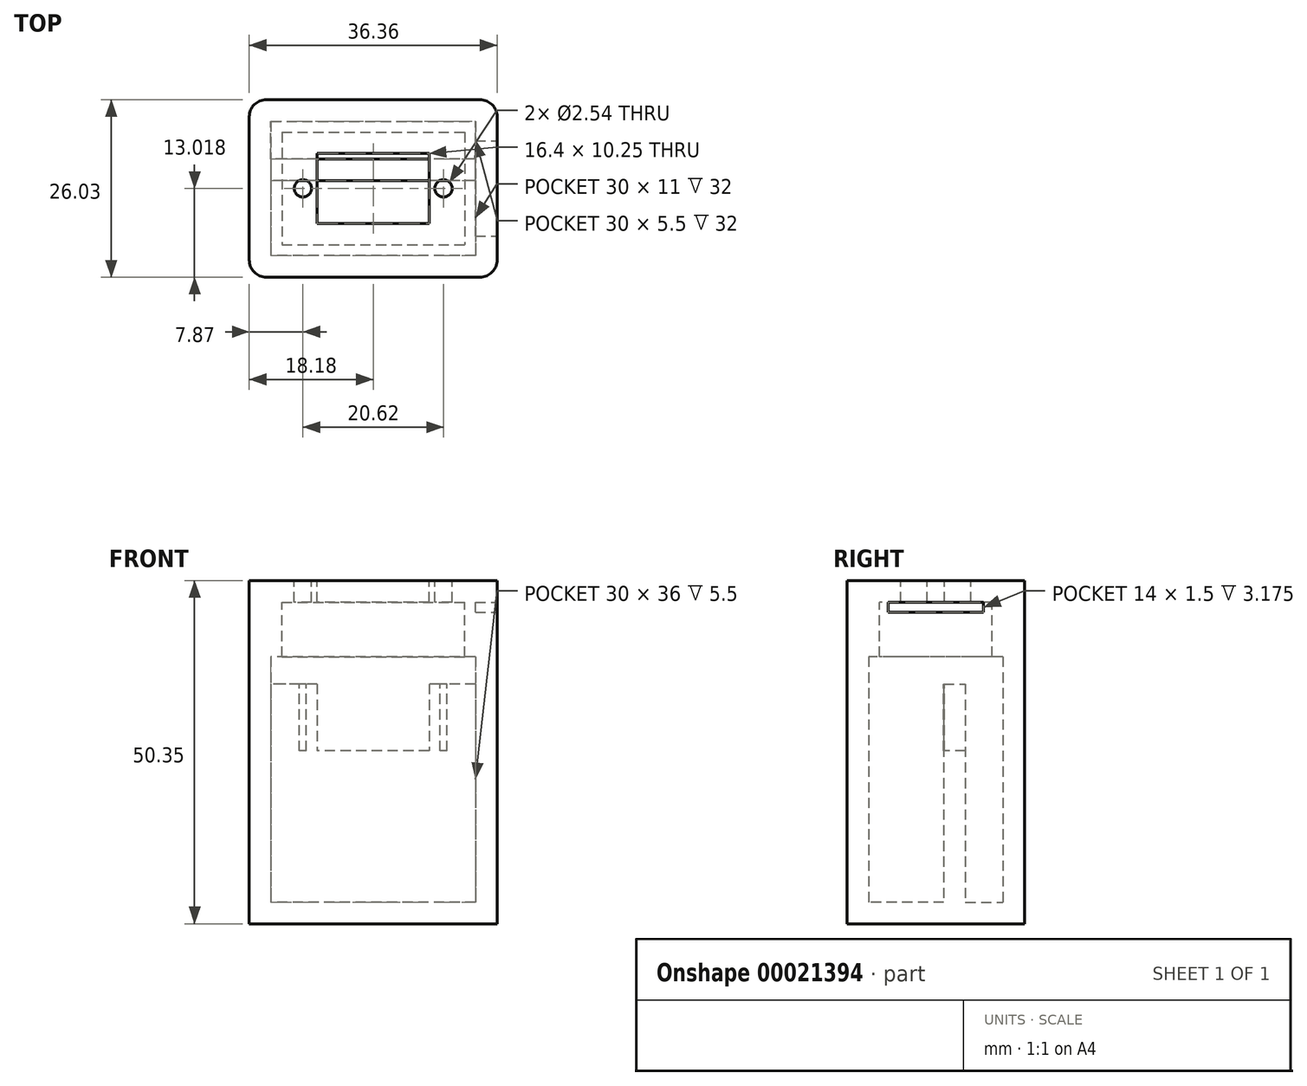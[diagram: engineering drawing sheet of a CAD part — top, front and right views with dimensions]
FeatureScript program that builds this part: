
annotation { "Feature Type Name" : "Feature", "Feature Type Description" : "" }
export const myFeature = defineFeature(function(context is Context, id is Id, definition is map)
    precondition{}
    {
        {
            var Q0;
            Q0=qCreatedBy(makeId("Top.planeOp"),FACE);
            var sketch = newSketch(context, id + "F0", { "sketchPlane" : qUnion([Q0])});
            skLineSegment(sketch, "E0.rect.bottom", {"start": v(15, 5.5) * mm, "end": v(-15, 5.5) * mm});
            skLineSegment(sketch, "E0.rect.top", {"start": v(15, -5.5) * mm, "end": v(-15, -5.5) * mm});
            skLineSegment(sketch, "E0.rect.left", {"start": v(15, 5.5) * mm, "end": v(15, -5.5) * mm});
            skLineSegment(sketch, "E0.rect.right", {"start": v(-15, 5.5) * mm, "end": v(-15, -5.5) * mm});
            skPoint(sketch, "E0.rect.middle", {"position": v(0, 0) * mm});
            skLineSegment(sketch, "E1.rect.bottom", {"start": v(18.18, 8.68) * mm, "end": v(-18.18, 8.68) * mm});
            skLineSegment(sketch, "E1.rect.top", {"start": v(18.18, -8.67) * mm, "end": v(-18.18, -8.68) * mm});
            skLineSegment(sketch, "E1.rect.left", {"start": v(18.18, 8.68) * mm, "end": v(18.18, -8.67) * mm});
            skLineSegment(sketch, "E1.rect.right", {"start": v(-18.18, 8.67) * mm, "end": v(-18.18, -8.68) * mm});
            skSolve(sketch);
        }
        {
            var Q0;
            Q0=makeQuery(id+"F0.imprint","IMPRINT",FACE,{"disambiguationData":[TD([[makeQuery(id+"F0.imprint","IMPRINT",EDGE,{"derivedFrom":sQuery(id+"F0.wireOp",EDGE,"E0.rect.bottom")}),-1.0]])]});
            extrude(context, id + "F1", {"entities" : qUnion([Q0]), "depth" : 44 * mm});
        }
        {
            var Q0;
            Q0=makeQuery(id+"F1.opExtrude","CAP_FACE",FACE,{"disambiguationData":[OSD([sQuery(id+"F0.wireOp",EDGE,"E0.rect.bottom"),sQuery(id+"F0.wireOp",EDGE,"E0.rect.top"),sQuery(id+"F0.wireOp",EDGE,"E0.rect.left"),sQuery(id+"F0.wireOp",EDGE,"E0.rect.right"),sQuery(id+"F0.wireOp",EDGE,"E1.rect.bottom"),sQuery(id+"F0.wireOp",EDGE,"E1.rect.top"),sQuery(id+"F0.wireOp",EDGE,"E1.rect.left"),sQuery(id+"F0.wireOp",EDGE,"E1.rect.right")])],"isStart":true});
            var sketch = newSketch(context, id + "F2", { "sketchPlane" : qUnion([Q0])});
            skLineSegment(sketch, "E2.bottom", {"start": v(-18.18, 8.68) * mm, "end": v(18.18, 8.68) * mm});
            skLineSegment(sketch, "E2.top", {"start": v(-18.18, -8.68) * mm, "end": v(18.18, -8.68) * mm});
            skLineSegment(sketch, "E2.left", {"start": v(-18.18, 8.68) * mm, "end": v(-18.18, -8.68) * mm});
            skLineSegment(sketch, "E2.right", {"start": v(18.18, 8.68) * mm, "end": v(18.18, -8.68) * mm});
            skSolve(sketch);
        }
        {
            var Q0;
            Q0 = qSketchRegion(id + "F2", true);
            extrude(context, id + "F3", {"entities" : qUnion([Q0]), "operationType" : NewBodyOperationType.ADD, "depth" : 3.17 * mm});
        }
        {
            var Q0;
            Q0=makeQuery(id+"F3.opExtrude","CAP_FACE",FACE,{"disambiguationData":[OSD([sQuery(id+"F2.wireOp",EDGE,"E2.bottom"),sQuery(id+"F2.wireOp",EDGE,"E2.top"),sQuery(id+"F2.wireOp",EDGE,"E2.left"),sQuery(id+"F2.wireOp",EDGE,"E2.right")])],"isStart":false});
            var sketch = newSketch(context, id + "F4", { "sketchPlane" : qUnion([Q0])});
            skLineSegment(sketch, "E3.bottom", {"start": v(-18.17, -8.67) * mm, "end": v(18.17, -8.67) * mm});
            skLineSegment(sketch, "E3.top", {"start": v(-18.17, -17.35) * mm, "end": v(18.17, -17.35) * mm});
            skLineSegment(sketch, "E3.left", {"start": v(-18.18, -8.68) * mm, "end": v(-18.18, -17.35) * mm});
            skLineSegment(sketch, "E3.right", {"start": v(18.18, -8.67) * mm, "end": v(18.18, -17.35) * mm});
            skLineSegment(sketch, "E4.0", {"start": v(-15, -5.5) * mm, "end": v(-15, 5.5) * mm});
            skLineSegment(sketch, "E5.0", {"start": v(15, -5.5) * mm, "end": v(15, 5.5) * mm});
            skLineSegment(sketch, "E6.bottom", {"start": v(-15, -8.67) * mm, "end": v(15, -8.67) * mm});
            skLineSegment(sketch, "E6.top", {"start": v(-15, -14.17) * mm, "end": v(15, -14.17) * mm});
            skLineSegment(sketch, "E6.left", {"start": v(-15, -8.67) * mm, "end": v(-15, -14.17) * mm});
            skLineSegment(sketch, "E6.right", {"start": v(15, -8.67) * mm, "end": v(15, -14.17) * mm});
            skSolve(sketch);
        }
        {
            var Q0;
            Q0=makeQuery(id+"F4.imprint","IMPRINT",FACE,{"disambiguationData":[TD([[makeQuery(id+"F4.imprint","IMPRINT",EDGE,{"derivedFrom":sQuery(id+"F4.wireOp",EDGE,"E3.top")}),1.0]])]});
            extrude(context, id + "F5", {"entities" : qUnion([Q0]), "operationType" : NewBodyOperationType.ADD, "oppositeDirection" : true, "depth" : 47.17 * mm});
        }
        {
            var Q0;
            Q0=makeQuery(id+"F5.boolean.opBoolean","MERGE",FACE,{"derivedFrom":[makeQuery(id+"F3.opExtrude","CAP_FACE",FACE,{"disambiguationData":[OSD([sQuery(id+"F2.wireOp",EDGE,"E2.bottom"),sQuery(id+"F2.wireOp",EDGE,"E2.top"),sQuery(id+"F2.wireOp",EDGE,"E2.left"),sQuery(id+"F2.wireOp",EDGE,"E2.right")])],"isStart":false}),makeQuery(id+"F5.opExtrude","CAP_FACE",FACE,{"disambiguationData":[OSD([sQuery(id+"F4.wireOp",EDGE,"E3.bottom"),sQuery(id+"F4.wireOp",EDGE,"E3.top"),sQuery(id+"F4.wireOp",EDGE,"E3.left"),sQuery(id+"F4.wireOp",EDGE,"E3.right"),sQuery(id+"F4.wireOp",EDGE,"E6.top"),sQuery(id+"F4.wireOp",EDGE,"E6.left"),sQuery(id+"F4.wireOp",EDGE,"E6.right")])],"isStart":true})]});
            var sketch = newSketch(context, id + "F6", { "sketchPlane" : qUnion([Q0])});
            skLineSegment(sketch, "E7.bottom", {"start": v(15, -8.68) * mm, "end": v(-15, -8.68) * mm});
            skLineSegment(sketch, "E7.top", {"start": v(15, -14.17) * mm, "end": v(-15, -14.17) * mm});
            skLineSegment(sketch, "E7.left", {"start": v(15, -8.68) * mm, "end": v(15, -14.17) * mm});
            skLineSegment(sketch, "E7.right", {"start": v(-15, -8.68) * mm, "end": v(-15, -14.17) * mm});
            skSolve(sketch);
        }
        {
            var Q0;
            Q0 = qSketchRegion(id + "F6", true);
            extrude(context, id + "F7", {"entities" : qUnion([Q0]), "operationType" : NewBodyOperationType.ADD, "oppositeDirection" : true, "depth" : 3.17 * mm});
        }
        {
            var Q0;
            Q0=makeQuery(id+"F5.opExtrude","SWEPT_EDGE",EDGE,{"disambiguationData":[OSD([sQuery(id+"F4.wireOp",EDGE,"E3.top"),sQuery(id+"F4.wireOp",EDGE,"E3.left")])]});
            var Q1;
            Q1=makeQuery(id+"F3.boolean.opBoolean","MERGE",EDGE,{"derivedFrom":[makeQuery(id+"F1.opExtrude","SWEPT_EDGE",EDGE,{"disambiguationData":[OSD([sQuery(id+"F0.wireOp",EDGE,"E1.rect.top"),sQuery(id+"F0.wireOp",EDGE,"E1.rect.right")])]}),makeQuery(id+"F3.opExtrude","SWEPT_EDGE",EDGE,{"disambiguationData":[OSD([sQuery(id+"F2.wireOp",EDGE,"E2.bottom"),sQuery(id+"F2.wireOp",EDGE,"E2.left")])]})]});
            var Q2;
            Q2=makeQuery(id+"F3.boolean.opBoolean","MERGE",EDGE,{"derivedFrom":[makeQuery(id+"F1.opExtrude","SWEPT_EDGE",EDGE,{"disambiguationData":[OSD([sQuery(id+"F0.wireOp",EDGE,"E1.rect.top"),sQuery(id+"F0.wireOp",EDGE,"E1.rect.left")])]}),makeQuery(id+"F3.opExtrude","SWEPT_EDGE",EDGE,{"disambiguationData":[OSD([sQuery(id+"F2.wireOp",EDGE,"E2.bottom"),sQuery(id+"F2.wireOp",EDGE,"E2.right")])]})]});
            var Q3;
            Q3=makeQuery(id+"F5.opExtrude","SWEPT_EDGE",EDGE,{"disambiguationData":[OSD([sQuery(id+"F4.wireOp",EDGE,"E3.top"),sQuery(id+"F4.wireOp",EDGE,"E3.right")])]});
            fillet(context, id + "F8", {"entities" : qUnion([Q0, Q1, Q2, Q3]), "radius" : 2.5 * mm, "tangentPropagation" : true, "allowEdgeOverflow" : false});
        }
        {
            var Q0;
            Q0=makeQuery(id+"F5.boolean.opBoolean","MERGE",FACE,{"derivedFrom":[makeQuery(id+"F1.opExtrude","CAP_FACE",FACE,{"disambiguationData":[OSD([sQuery(id+"F0.wireOp",EDGE,"E0.rect.bottom"),sQuery(id+"F0.wireOp",EDGE,"E0.rect.top"),sQuery(id+"F0.wireOp",EDGE,"E0.rect.left"),sQuery(id+"F0.wireOp",EDGE,"E0.rect.right"),sQuery(id+"F0.wireOp",EDGE,"E1.rect.bottom"),sQuery(id+"F0.wireOp",EDGE,"E1.rect.top"),sQuery(id+"F0.wireOp",EDGE,"E1.rect.left"),sQuery(id+"F0.wireOp",EDGE,"E1.rect.right")])],"isStart":false}),makeQuery(id+"F5.opExtrude","CAP_FACE",FACE,{"disambiguationData":[OSD([sQuery(id+"F4.wireOp",EDGE,"E3.bottom"),sQuery(id+"F4.wireOp",EDGE,"E3.top"),sQuery(id+"F4.wireOp",EDGE,"E3.left"),sQuery(id+"F4.wireOp",EDGE,"E3.right"),sQuery(id+"F4.wireOp",EDGE,"E6.top"),sQuery(id+"F4.wireOp",EDGE,"E6.left"),sQuery(id+"F4.wireOp",EDGE,"E6.right")])],"isStart":false})]});
            var sketch = newSketch(context, id + "F9", { "sketchPlane" : qUnion([Q0])});
            skLineSegment(sketch, "E8.rect.bottom", {"start": v(15, 11.34) * mm, "end": v(21.35, 11.34) * mm});
            skLineSegment(sketch, "E8.rect.top", {"start": v(15, -2.66) * mm, "end": v(21.35, -2.66) * mm});
            skLineSegment(sketch, "E8.rect.left", {"start": v(15, 11.34) * mm, "end": v(15, -2.66) * mm});
            skLineSegment(sketch, "E8.rect.right", {"start": v(21.35, 11.34) * mm, "end": v(21.35, -2.66) * mm});
            skPoint(sketch, "E8.rect.middle", {"position": v(18.18, 4.34) * mm});
            skSolve(sketch);
        }
        {
            var Q0;
            Q0 = qSketchRegion(id + "F9", true);
            extrude(context, id + "F10", {"entities" : qUnion([Q0]), "operationType" : NewBodyOperationType.REMOVE, "oppositeDirection" : true, "depth" : 1.5 * mm});
        }
        {
            var Q0;
            Q0=makeQuery(id+"F5.boolean.opBoolean","MERGE",FACE,{"derivedFrom":[makeQuery(id+"F1.opExtrude","CAP_FACE",FACE,{"disambiguationData":[OSD([sQuery(id+"F0.wireOp",EDGE,"E0.rect.bottom"),sQuery(id+"F0.wireOp",EDGE,"E0.rect.top"),sQuery(id+"F0.wireOp",EDGE,"E0.rect.left"),sQuery(id+"F0.wireOp",EDGE,"E0.rect.right"),sQuery(id+"F0.wireOp",EDGE,"E1.rect.bottom"),sQuery(id+"F0.wireOp",EDGE,"E1.rect.top"),sQuery(id+"F0.wireOp",EDGE,"E1.rect.left"),sQuery(id+"F0.wireOp",EDGE,"E1.rect.right")])],"isStart":false}),makeQuery(id+"F5.opExtrude","CAP_FACE",FACE,{"disambiguationData":[OSD([sQuery(id+"F4.wireOp",EDGE,"E3.bottom"),sQuery(id+"F4.wireOp",EDGE,"E3.top"),sQuery(id+"F4.wireOp",EDGE,"E3.left"),sQuery(id+"F4.wireOp",EDGE,"E3.right"),sQuery(id+"F4.wireOp",EDGE,"E6.top"),sQuery(id+"F4.wireOp",EDGE,"E6.left"),sQuery(id+"F4.wireOp",EDGE,"E6.right")])],"isStart":false})]});
            var sketch = newSketch(context, id + "F11", { "sketchPlane" : qUnion([Q0])});
            skLineSegment(sketch, "E9.bottom", {"start": v(-15, 8.68) * mm, "end": v(15, 8.68) * mm});
            skLineSegment(sketch, "E9.top", {"start": v(-15, 5.5) * mm, "end": v(15, 5.5) * mm});
            skLineSegment(sketch, "E9.left", {"start": v(-15, 8.68) * mm, "end": v(-15, 5.5) * mm});
            skLineSegment(sketch, "E9.right", {"start": v(15, 8.68) * mm, "end": v(15, 5.5) * mm});
            skSolve(sketch);
        }
        {
            var Q0;
            Q0=makeQuery(id+"F11.imprint","IMPRINT",FACE,{"disambiguationData":[TD([[makeQuery(id+"F11.imprint","IMPRINT",EDGE,{"derivedFrom":sQuery(id+"F11.wireOp",EDGE,"E9.bottom")}),1.0]])]});
            extrude(context, id + "F12", {"entities" : qUnion([Q0]), "operationType" : NewBodyOperationType.REMOVE, "oppositeDirection" : true, "depth" : 12 * mm});
        }
        {
            var Q0;
            Q0=makeQuery(id+"F5.boolean.opBoolean","MERGE",FACE,{"derivedFrom":[makeQuery(id+"F1.opExtrude","CAP_FACE",FACE,{"disambiguationData":[OSD([sQuery(id+"F0.wireOp",EDGE,"E0.rect.bottom"),sQuery(id+"F0.wireOp",EDGE,"E0.rect.top"),sQuery(id+"F0.wireOp",EDGE,"E0.rect.left"),sQuery(id+"F0.wireOp",EDGE,"E0.rect.right"),sQuery(id+"F0.wireOp",EDGE,"E1.rect.bottom"),sQuery(id+"F0.wireOp",EDGE,"E1.rect.top"),sQuery(id+"F0.wireOp",EDGE,"E1.rect.left"),sQuery(id+"F0.wireOp",EDGE,"E1.rect.right")])],"isStart":false}),makeQuery(id+"F5.opExtrude","CAP_FACE",FACE,{"disambiguationData":[OSD([sQuery(id+"F4.wireOp",EDGE,"E3.bottom"),sQuery(id+"F4.wireOp",EDGE,"E3.top"),sQuery(id+"F4.wireOp",EDGE,"E3.left"),sQuery(id+"F4.wireOp",EDGE,"E3.right"),sQuery(id+"F4.wireOp",EDGE,"E6.top"),sQuery(id+"F4.wireOp",EDGE,"E6.left"),sQuery(id+"F4.wireOp",EDGE,"E6.right")])],"isStart":false})]});
            var sketch = newSketch(context, id + "F13", { "sketchPlane" : qUnion([Q0])});
            skLineSegment(sketch, "E10.bottom", {"start": v(-15.68, 17.35) * mm, "end": v(15.68, 17.35) * mm});
            skLineSegment(sketch, "E10.top", {"start": v(-15.68, -8.67) * mm, "end": v(15.68, -8.67) * mm});
            skLineSegment(sketch, "E10.left", {"start": v(-18.18, 14.85) * mm, "end": v(-18.18, -6.17) * mm});
            skLineSegment(sketch, "E10.right", {"start": v(18.18, 14.85) * mm, "end": v(18.18, -6.17) * mm});
            skPoint(sketch, "E11.visualSharp", {"position": v(-18.18, 17.35) * mm});
            skArc(sketch, "E11.filletArc", {"start": v(-15.68, 17.35) * mm, "mid": v(-17.44, 16.62) * mm, "end": v(-18.18, 14.85) * mm});
            skPoint(sketch, "E12.visualSharp", {"position": v(18.18, 17.35) * mm});
            skArc(sketch, "E12.filletArc", {"start": v(18.18, 14.85) * mm, "mid": v(17.44, 16.62) * mm, "end": v(15.68, 17.35) * mm});
            skPoint(sketch, "E13.visualSharp", {"position": v(18.18, -8.67) * mm});
            skArc(sketch, "E13.filletArc", {"start": v(15.68, -8.67) * mm, "mid": v(17.44, -7.94) * mm, "end": v(18.18, -6.17) * mm});
            skPoint(sketch, "E14.visualSharp", {"position": v(-18.18, -8.67) * mm});
            skArc(sketch, "E14.filletArc", {"start": v(-18.18, -6.17) * mm, "mid": v(-17.44, -7.94) * mm, "end": v(-15.68, -8.67) * mm});
            skSolve(sketch);
        }
        {
            var Q0;
            Q0 = qSketchRegion(id + "F13", true);
            extrude(context, id + "F14", {"entities" : qUnion([Q0]), "depth" : 3.17 * mm});
        }
        {
            var Q0;
            Q0=makeQuery(id+"F5.boolean.opBoolean","MERGE",FACE,{"derivedFrom":[makeQuery(id+"F1.opExtrude","CAP_FACE",FACE,{"disambiguationData":[OSD([sQuery(id+"F0.wireOp",EDGE,"E0.rect.bottom"),sQuery(id+"F0.wireOp",EDGE,"E0.rect.top"),sQuery(id+"F0.wireOp",EDGE,"E0.rect.left"),sQuery(id+"F0.wireOp",EDGE,"E0.rect.right"),sQuery(id+"F0.wireOp",EDGE,"E1.rect.bottom"),sQuery(id+"F0.wireOp",EDGE,"E1.rect.top"),sQuery(id+"F0.wireOp",EDGE,"E1.rect.left"),sQuery(id+"F0.wireOp",EDGE,"E1.rect.right")])],"isStart":false}),makeQuery(id+"F5.opExtrude","CAP_FACE",FACE,{"disambiguationData":[OSD([sQuery(id+"F4.wireOp",EDGE,"E3.bottom"),sQuery(id+"F4.wireOp",EDGE,"E3.top"),sQuery(id+"F4.wireOp",EDGE,"E3.left"),sQuery(id+"F4.wireOp",EDGE,"E3.right"),sQuery(id+"F4.wireOp",EDGE,"E6.top"),sQuery(id+"F4.wireOp",EDGE,"E6.left"),sQuery(id+"F4.wireOp",EDGE,"E6.right")])],"isStart":false})]});
            var sketch = newSketch(context, id + "F15", { "sketchPlane" : qUnion([Q0])});
            skLineSegment(sketch, "E15.bottom", {"start": v(-15, 14.17) * mm, "end": v(15, 14.17) * mm});
            skLineSegment(sketch, "E15.top", {"start": v(-15, -5.5) * mm, "end": v(15, -5.5) * mm});
            skLineSegment(sketch, "E15.left", {"start": v(-15, 14.17) * mm, "end": v(-15, -5.5) * mm});
            skLineSegment(sketch, "E15.right", {"start": v(15, 14.17) * mm, "end": v(15, -5.5) * mm});
            skLineSegment(sketch, "E16.bottom", {"start": v(-13.4, 12.57) * mm, "end": v(13.4, 12.57) * mm});
            skLineSegment(sketch, "E16.top", {"start": v(-13.4, -3.9) * mm, "end": v(13.4, -3.9) * mm});
            skLineSegment(sketch, "E16.left", {"start": v(-13.4, 12.57) * mm, "end": v(-13.4, -3.9) * mm});
            skLineSegment(sketch, "E16.right", {"start": v(13.4, 12.57) * mm, "end": v(13.4, -3.9) * mm});
            skSolve(sketch);
        }
        {
            var Q0;
            {var subQ4=sQuery(id+"F15.wireOp",EDGE,"E15.bottom");Q0=makeQuery(id+"F15.imprint","IMPRINT",FACE,{"disambiguationData":[TD([[makeQuery(id+"F15.imprint","IMPRINT",EDGE,{"derivedFrom":subQ4}),-1.0]])]});}
            extrude(context, id + "F16", {"entities" : qUnion([Q0]), "operationType" : NewBodyOperationType.ADD, "oppositeDirection" : true, "depth" : 8 * mm});
        }
        {
            var Q0;
            Q0=makeQuery(id+"F14.opExtrude","CAP_FACE",FACE,{"disambiguationData":[OSD([sQuery(id+"F13.wireOp",EDGE,"E10.bottom"),sQuery(id+"F13.wireOp",EDGE,"E10.top"),sQuery(id+"F13.wireOp",EDGE,"E10.left"),sQuery(id+"F13.wireOp",EDGE,"E10.right"),sQuery(id+"F13.wireOp",EDGE,"E11.filletArc"),sQuery(id+"F13.wireOp",EDGE,"E12.filletArc"),sQuery(id+"F13.wireOp",EDGE,"E13.filletArc"),sQuery(id+"F13.wireOp",EDGE,"E14.filletArc")])],"isStart":false});
            var sketch = newSketch(context, id + "F17", { "sketchPlane" : qUnion([Q0])});
            skLineSegment(sketch, "E17.rect.bottom", {"start": v(8.2, 9.46) * mm, "end": v(-8.2, 9.46) * mm});
            skLineSegment(sketch, "E17.rect.top", {"start": v(8.2, -0.79) * mm, "end": v(-8.2, -0.79) * mm});
            skLineSegment(sketch, "E17.rect.left", {"start": v(8.2, 9.46) * mm, "end": v(8.2, -0.79) * mm});
            skLineSegment(sketch, "E17.rect.right", {"start": v(-8.2, 9.46) * mm, "end": v(-8.2, -0.79) * mm});
            skPoint(sketch, "E17.rect.middle", {"position": v(0, 4.34) * mm});
            skLineSegment(sketch, "E18", {"start": v(0, 4.34) * mm, "end": v(-10.31, 4.34) * mm});
            skLineSegment(sketch, "E19", {"start": v(0, 4.34) * mm, "end": v(10.31, 4.34) * mm});
            skCircle(sketch, "E20", {"center": v(10.31, 4.34) * mm, "radius": 1.27 * mm});
            skCircle(sketch, "E21", {"center": v(-10.31, 4.34) * mm, "radius": 1.27 * mm});
            skSolve(sketch);
        }
        {
            var Q0;
            Q0 = qSketchRegion(id + "F17", true);
            var Q1;
            Q1=makeQuery(id+"F17.imprint","IMPRINT",FACE,{"disambiguationData":[TD([[makeQuery(id+"F17.imprint","IMPRINT",EDGE,{"derivedFrom":sQuery(id+"F17.wireOp",EDGE,"E21")}),1.0]])]});
            extrude(context, id + "F18", {"entities" : qUnion([Q0, Q1]), "operationType" : NewBodyOperationType.REMOVE, "oppositeDirection" : true, "depth" : 25 * mm});
        }
    });
